# Revit family: SQI-HP
name_source: partatom
category: Mechanical Equipment
units: mm (PartAtom-declared; Revit-internal decimal feet)

## family parameters
Always vertical = Yes
Cut with Voids When Loaded = No
Part Type = Normal
Room Calculation Point = No
Round Connector Dimension = Use Diameter
Shared = No
Work Plane-Based = No

## types (15) — shared parameters
0 = 0"
1" = 1"
1.5 = 1 1/2"
2" = 2"
2' = 24"
3" = 3"
4" = 4"
Manufacturer = Loren Cook Company
Model = SQI-HP
ONE EIGTH = 1/8"
Type Comments = Square Centrifugal High Pressure Inline Belt Drive
URL = www.lorencook.com

## per-type parameters (varying)
| type | (A+.25")/2 | -C/2 | A | A+.25" | A/2 | B | B/2 | C | C-.125" | C/2 | D | D/2 | D/3 | D/6 | E | E/2 | MOTOR_DEPTH |
| 90_SQI-HP | 7 11/32" | -8 13/32" | 14 7/16" | 14 11/16" | 7 7/32" | 14 3/8" | 7 3/16" | 16 13/16" | 16 11/16" | 8 13/32" | 17 1/2" | 8 3/4" | 5 27/32" | 2 29/32" | 14 5/16" | 7 5/32" | -16" |
| 120_SQI-HP | 8 13/16" | -10 3/32" | 17 3/8" | 17 5/8" | 8 11/16" | 17 3/4" | 8 7/8" | 20 3/16" | 20 1/16" | 10 3/32" | 20 1/2" | 10 1/4" | 6 27/32" | 3 13/32" | 14 5/16" | 7 5/32" | -18" |
| 135_SQI-HP | 9 7/8" | -11 11/32" | 19 1/2" | 19 3/4" | 9 3/4" | 20 1/4" | 10 1/8" | 22 11/16" | 22 9/16" | 11 11/32" | 22 5/8" | 11 5/16" | 7 17/32" | 3 25/32" | 14 5/16" | 7 5/32" | -18" |
| 150_SQI-HP | 10 15/16" | -12 5/8" | 21 5/8" | 21 7/8" | 10 13/16" | 22 13/16" | 11 13/32" | 25 1/4" | 25 1/8" | 12 5/8" | 24 3/4" | 12 3/8" | 8 1/4" | 4 1/8" | 14 5/16" | 7 5/32" | -18" |
| 165_SQI-HP | 12 1/32" | -13 7/8" | 23 13/16" | 24 1/16" | 11 29/32" | 25 5/16" | 12 21/32" | 27 3/4" | 27 5/8" | 13 7/8" | 26 15/16" | 13 15/32" | 8 31/32" | 4 1/2" | 14 5/16" | 7 5/32" | -20" |
| 180_SQI-HP | 13 1/8" | -15 1/8" | 26" | 26 1/4" | 13" | 27 13/16" | 13 29/32" | 30 1/4" | 30 1/8" | 15 1/8" | 29 1/8" | 14 9/16" | 9 23/32" | 4 27/32" | 14 5/16" | 7 5/32" | -20" |
| 195_SQI-HP | 14 7/32" | -16 3/8" | 28 3/16" | 28 7/16" | 14 3/32" | 30 1/8" | 15 1/16" | 32 3/4" | 32 5/8" | 16 3/8" | 31 5/16" | 15 21/32" | 10 7/16" | 5 7/32" | 14 5/16" | 7 5/32" | -22" |
| 210_SQI-HP | 15 5/16" | -17 5/8" | 30 3/8" | 30 5/8" | 15 3/16" | 32 5/8" | 16 5/16" | 35 1/4" | 35 1/8" | 17 5/8" | 33 1/2" | 16 3/4" | 11 5/32" | 5 19/32" | 14 5/16" | 7 5/32" | -22" |
| 225_SQI-HP | 16 3/8" | -18 29/32" | 32 1/2" | 32 3/4" | 16 1/4" | 35 3/16" | 17 19/32" | 37 13/16" | 37 11/16" | 18 29/32" | 35 5/8" | 17 13/16" | 11 7/8" | 5 15/16" | 17 1/2" | 8 3/4" | -22" |
| 245_SQI-HP | 17 13/16" | -20 19/32" | 35 3/8" | 35 5/8" | 17 11/16" | 38 9/16" | 19 9/32" | 41 3/16" | 41 1/16" | 20 19/32" | 38 1/2" | 19 1/4" | 12 27/32" | 6 13/32" | 17 1/2" | 8 3/4" | -22" |
| 270_SQI-HP | 19 5/8" | -22 11/16" | 39" | 39 1/4" | 19 1/2" | 42 3/4" | 21 3/8" | 45 3/8" | 45 1/4" | 22 11/16" | 42 1/8" | 21 1/16" | 14 1/32" | 7 1/32" | 17 1/2" | 8 3/4" | -22 11/16" |
| 300_SQI-HP | 21 27/32" | -25 7/32" | 43 7/16" | 43 11/16" | 21 23/32" | 47 13/16" | 23 29/32" | 50 7/16" | 50 5/16" | 25 7/32" | 46 1/2" | 23 1/4" | 15 1/2" | 7 3/4" | 17 1/2" | 8 3/4" | -25 7/32" |
| 330_SQI-HP | 23 15/16" | -27 23/32" | 47 5/8" | 47 7/8" | 23 13/16" | 52 13/16" | 26 13/32" | 55 7/16" | 55 5/16" | 27 23/32" | 50 3/4" | 25 3/8" | 16 29/32" | 8 15/32" | 17 1/2" | 8 3/4" | -27 23/32" |
| 365_SQI-HP | 26 1/2" | -30 11/16" | 52 3/4" | 53" | 26 3/8" | 58 15/16" | 29 15/32" | 61 3/8" | 61 1/4" | 30 11/16" | 55 7/8" | 27 15/16" | 18 5/8" | 9 5/16" | 17 1/2" | 8 3/4" | -30 11/16" |
| 402_SQI-HP | 29 1/4" | -32 1/8" | 58 1/4" | 58 1/2" | 29 1/8" | 61 3/4" | 30 7/8" | 64 1/4" | 64 1/8" | 32 1/8" | 61 1/2" | 30 3/4" | 20 1/2" | 10 1/4" | 17 1/2" | 8 3/4" | -32 1/8" |

## geometry (parser evidence)
native form markers: Sweep x2
no freeform markers — native parametric forms only
